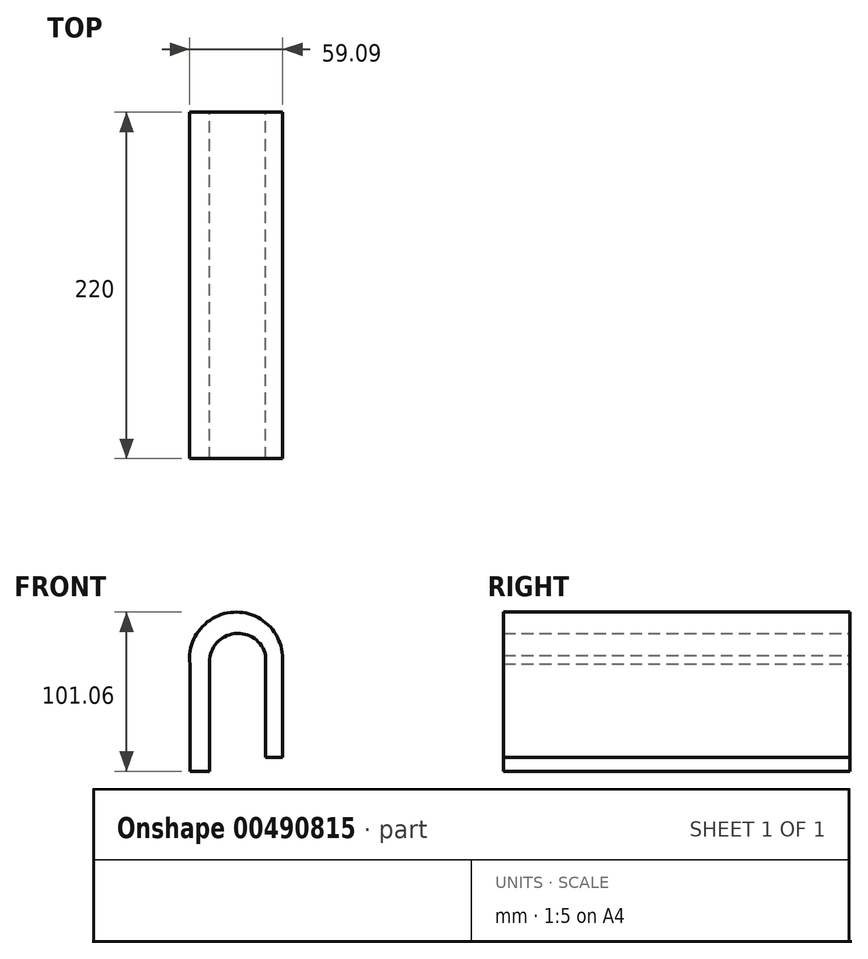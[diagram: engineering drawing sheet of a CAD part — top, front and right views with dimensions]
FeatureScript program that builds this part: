
annotation { "Feature Type Name" : "Feature", "Feature Type Description" : "" }
export const myFeature = defineFeature(function(context is Context, id is Id, definition is map)
    precondition{}
    {
        {
            var Q0;
            Q0=qCreatedBy(makeId("Front.planeOp"),FACE);
            var sketch = newSketch(context, id + "F0", { "sketchPlane" : qUnion([Q0])});
            skLineSegment(sketch, "E0", {"start": v(-32.84, 29.76) * mm, "end": v(-32.84, -38.44) * mm});
            skLineSegment(sketch, "E1", {"start": v(-32.84, -38.44) * mm, "end": v(-20.38, -38.44) * mm});
            skLineSegment(sketch, "E2", {"start": v(-20.38, -38.44) * mm, "end": v(-20.38, 31) * mm});
            skLineSegment(sketch, "E3", {"start": v(15.35, 35.23) * mm, "end": v(15.35, -29.57) * mm});
            skLineSegment(sketch, "E4", {"start": v(15.35, -29.57) * mm, "end": v(26.06, -29.57) * mm});
            skLineSegment(sketch, "E5", {"start": v(26.06, -29.57) * mm, "end": v(26.06, 33.08) * mm});
            skArc(sketch, "E6", {"start": v(26.06, 33.08) * mm, "mid": v(-5.15, 62.58) * mm, "end": v(-32.84, 29.76) * mm});
            skArc(sketch, "E7", {"start": v(15.35, 35.23) * mm, "mid": v(-4.39, 49) * mm, "end": v(-20.38, 31) * mm});
            skSolve(sketch);
        }
        {
            var Q0;
            Q0=makeQuery(id+"F0.imprint","IMPRINT",FACE,{"disambiguationData":[TD([[makeQuery(id+"F0.imprint","IMPRINT",EDGE,{"derivedFrom":sQuery(id+"F0.wireOp",EDGE,"E0")}),1.0]])]});
            extrude(context, id + "F1", {"entities" : qUnion([Q0]), "depth" : 220 * mm});
        }
    });
